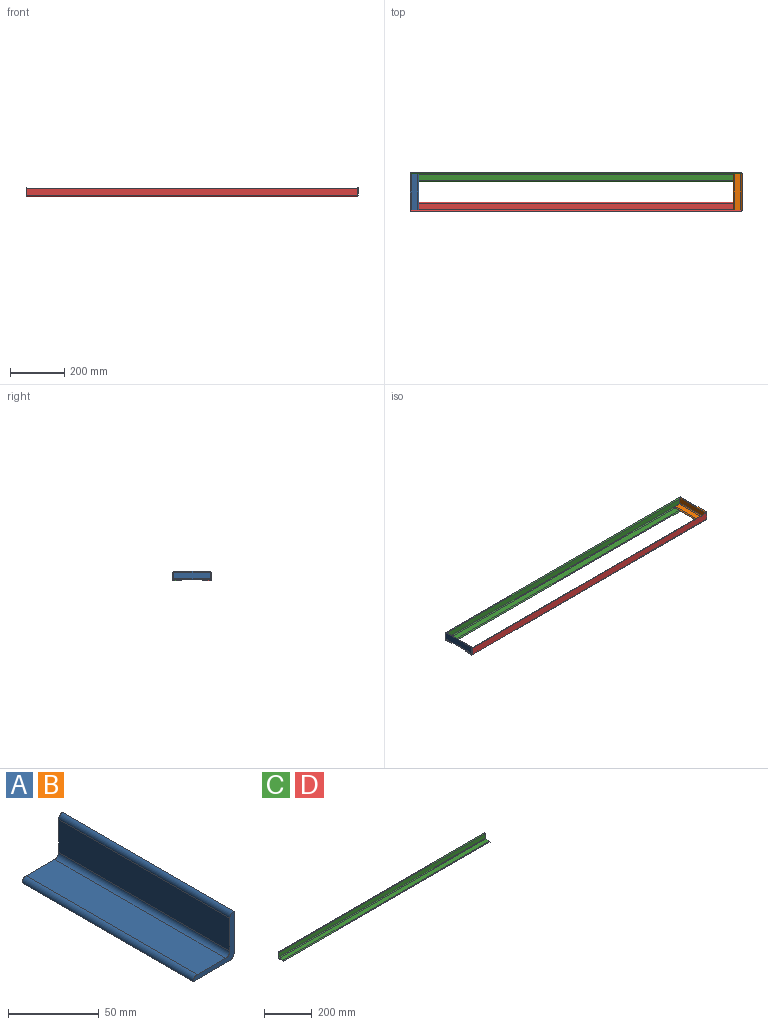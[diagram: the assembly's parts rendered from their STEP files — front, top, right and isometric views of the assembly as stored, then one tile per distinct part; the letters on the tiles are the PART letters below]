
ASSEMBLY  parts=4 mates=7
PART A: 10 faces, bbox 31.8x133.4x31.8 mm
  f0: cylinder r=3.17mm len=133.35mm, axis (0,1,0), area 665.1mm2, adj f1,f7,f8,f9
  f1: plane 133.35x22.23mm, normal (0,0,1), area 2963.7mm2, adj f0,f2,f8,f9
  f2: cylinder r=3.17mm len=133.35mm, axis (0,1,0), area 665.1mm2, adj f1,f3,f8,f9
  f3: plane 133.35x28.58mm, normal (0,0,-1), area 3810.5mm2, adj f2,f4,f8,f9
  f4: cylinder r=3.17mm len=133.35mm, axis (0,1,0), area 665.1mm2, adj f3,f5,f8,f9
  f5: plane 133.35x28.58mm, normal (1,0,0), area 3810.5mm2, adj f4,f6,f8,f9
  f6: cylinder r=3.17mm len=133.35mm, axis (0,1,0), area 665.1mm2, adj f5,f7,f8,f9
  f7: plane 133.35x22.23mm, normal (-1,0,0), area 2963.7mm2, adj f0,f6,f8,f9
  f8: plane 31.75x31.75mm, normal (0,-1,0), area 187.2mm2, adj f0,f1,f2,f3,f4,f5,f6,f7
  f9: plane 31.75x31.75mm, normal (0,1,0), area 187.2mm2, adj f0,f1,f2,f3,f4,f5,f6,f7
PART B: same geometry as A
PART C: 10 faces, bbox 1219.2x31.8x31.8 mm
  f0: cylinder r=3.17mm len=1219.2mm, axis (1,0,0), area 6080.5mm2, adj f1,f7,f8,f9
  f1: plane 1219.2x22.23mm, normal (0,0,1), area 27096.7mm2, adj f0,f2,f8,f9
  f2: cylinder r=3.17mm len=1219.2mm, axis (1,0,0), area 6080.5mm2, adj f1,f3,f8,f9
  f3: plane 1219.2x28.58mm, normal (0,0,-1), area 34838.6mm2, adj f2,f4,f8,f9
  f4: cylinder r=3.17mm len=1219.2mm, axis (1,0,0), area 6080.5mm2, adj f3,f5,f8,f9
  f5: plane 1219.2x28.58mm, normal (0,1,0), area 34838.6mm2, adj f4,f6,f8,f9
  f6: cylinder r=3.17mm len=1219.2mm, axis (1,0,0), area 6080.5mm2, adj f5,f7,f8,f9
  f7: plane 1219.2x22.23mm, normal (0,-1,0), area 27096.7mm2, adj f0,f6,f8,f9
  f8: plane 31.75x31.75mm, normal (-1,0,0), area 187.2mm2, adj f0,f1,f2,f3,f4,f5,f6,f7
  f9: plane 31.75x31.75mm, normal (1,0,0), area 187.2mm2, adj f0,f1,f2,f3,f4,f5,f6,f7
PART D: same geometry as C
PLACE A rot(axis=(0,1,0),90deg) t=(-819.23,8.76,88.64)mm
PLACE B t=(381.51,8.76,88.64)mm
PLACE C t=(390.74,-980.67,371.88)mm
PLACE D rot(axis=(-1,0,0),90deg) t=(390.74,167.88,1068.84)mm
MATE planar C.f7 <-> B.f9  axis (0,-1,0) through (390.74,8.76,93.7)mm
MATE planar B.f5 <-> D.f9  axis (1,0,0) through (390.74,-57.92,96.87)mm
MATE planar A.f3 <-> C.f8  axis (-1,0,0) through (-828.46,-57.92,96.87)mm
MATE planar A.f8 <-> D.f1  axis (0,-1,0) through (-828.46,-124.59,96.87)mm
MATE planar B.f8 <-> D.f1  axis (0,-1,0) through (390.74,-124.59,96.87)mm
MATE planar B.f5 <-> C.f9  axis (1,0,0) through (390.74,-57.92,96.87)mm
MATE planar D.f5 <-> C.f3  axis (0,0,-1) through (-218.86,-110.31,76.24)mm
